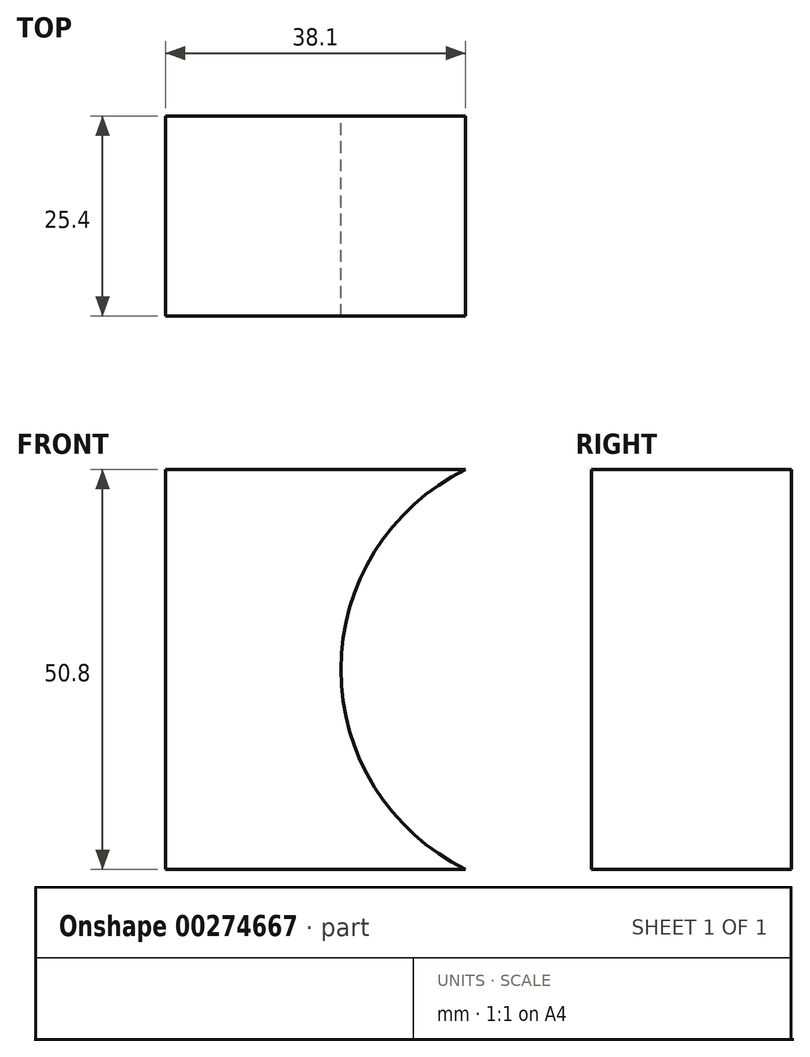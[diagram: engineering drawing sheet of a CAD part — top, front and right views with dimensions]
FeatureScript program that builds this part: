
annotation { "Feature Type Name" : "Feature", "Feature Type Description" : "" }
export const myFeature = defineFeature(function(context is Context, id is Id, definition is map)
    precondition{}
    {
        {
            var Q0;
            Q0=qCreatedBy(makeId("Front.planeOp"),FACE);
            var sketch = newSketch(context, id + "F0", { "sketchPlane" : qUnion([Q0])});
            skLineSegment(sketch, "E0", {"start": v(-51.37, 48.9) * mm, "end": v(-51.37, -1.9) * mm});
            skLineSegment(sketch, "E1", {"start": v(-51.37, -1.9) * mm, "end": v(-13.27, -1.9) * mm});
            skLineSegment(sketch, "E2", {"start": v(-51.37, 48.9) * mm, "end": v(-13.27, 48.9) * mm});
            skArc(sketch, "E3", {"start": v(-13.27, 48.9) * mm, "mid": v(-29.1, 23.5) * mm, "end": v(-13.27, -1.9) * mm});
            skSolve(sketch);
        }
        {
            var Q0;
            Q0 = qSketchRegion(id + "F0", true);
            extrude(context, id + "F1", {"entities" : qUnion([Q0]), "depth" : 25.4 * mm});
        }
    });
